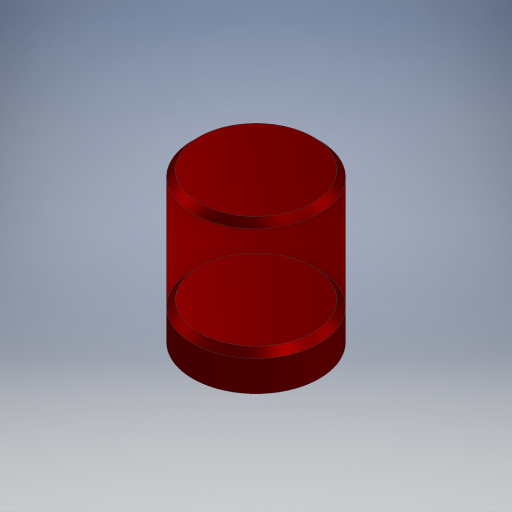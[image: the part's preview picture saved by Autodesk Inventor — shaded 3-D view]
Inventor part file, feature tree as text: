
AUTODESK INVENTOR PART (.ipt)
format: ipt  version: 2024.2 (Build 282272000, 272)  size: 649,728 bytes
history: native  units: in
note: dims shown in document units (in); Inventor stores cm internally (conversion verified against a paired STEP export)
features: extrude x6, sketch x6, projected_geometry x6, chamfer x1
ambient origin geometry x8: Origin, YZ Plane, XZ Plane, XY Plane, X Axis, Y Axis, Z Axis, Center Point
bodies: Solid1 (feature_tree)
feature tree (19):
  extrude  "Extrusion1"  Depth=2.3in
  extrude  "Extrusion2"  Depth=2.263in
  extrude  "Extrusion3"  Depth=0.125in
  chamfer  "Chamfer1"  Distance=0.586in
  extrude  "Extrusion5"  Depth=0.125in TaperAngle=0.0deg
  extrude  "Extrusion7"  Depth=0.616in TaperAngle=0.0deg
  extrude  "Extrusion8"  Depth=0.495in
  sketch  "Sketch1"  dims[d0=2.3in d1=2.3in]
  sketch  "Sketch2"  dims[d2=2.263in d3=2.263in]
  projected_geometry  "Projected Loop1"
  projected_geometry  "Projected Loop2"
  sketch  "Sketch3"  dims[d4=0.125in d5=0.125in d6=0.586in d7=0.0in]
  projected_geometry  "Projected Loop3"
  projected_geometry  "Projected Loop4"
  sketch  "Sketch5"  dims[d8=0.03in d9=0.0in d10=0.125in d11=0.0in]
  projected_geometry  "Projected Loop6"
  projected_geometry  "Projected Loop7"
  sketch  "Sketch7"  dims[d12=0.125in d13=0.125in d14=45.0deg d55=0.616in d56=0.0in]
  sketch  "Sketch8"  dims[d59=3.2004in d60=0.495in d61=0.4892in d62=0.08in d63=0.0417in d64=0.0394in d65=0.0in d66=0.0394in d67=0.0in]
